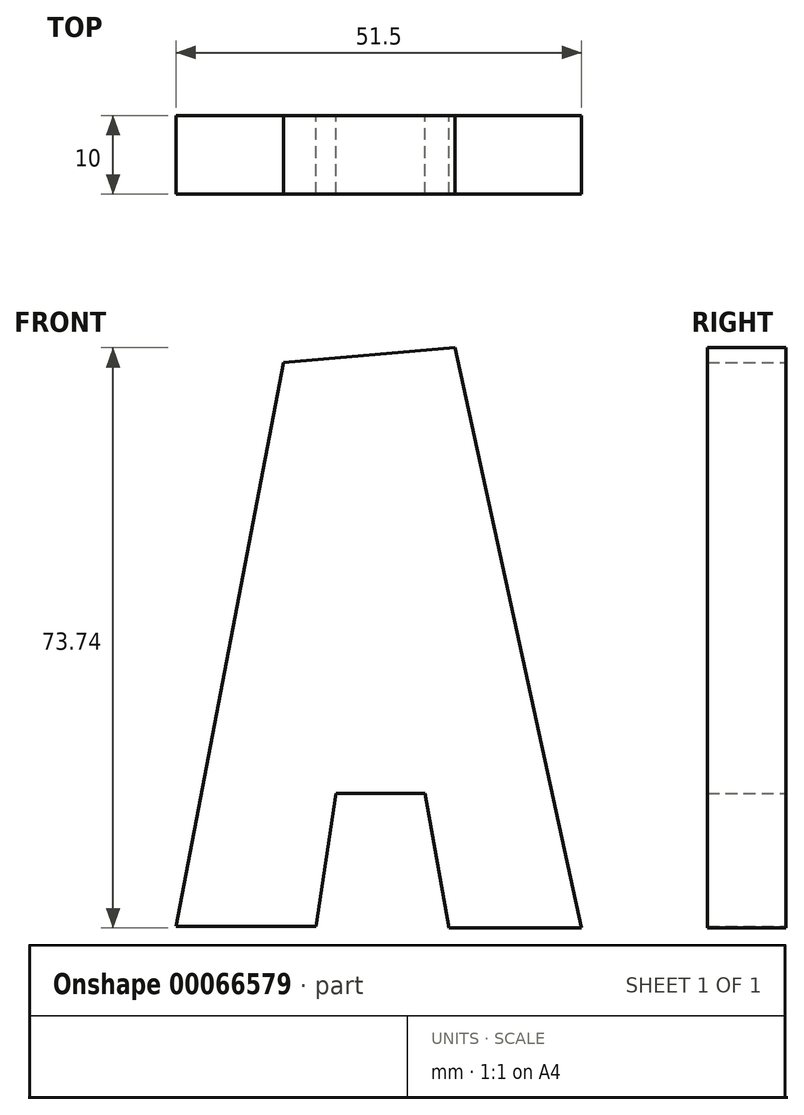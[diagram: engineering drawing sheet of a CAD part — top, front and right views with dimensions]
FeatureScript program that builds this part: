
annotation { "Feature Type Name" : "Feature", "Feature Type Description" : "" }
export const myFeature = defineFeature(function(context is Context, id is Id, definition is map)
    precondition{}
    {
        {
            var Q0;
            Q0=qCreatedBy(makeId("Front.planeOp"),FACE);
            var sketch = newSketch(context, id + "F0", { "sketchPlane" : qUnion([Q0])});
            skLineSegment(sketch, "E0", {"start": v(-11.08, 33.6) * mm, "end": v(-24.7, -37.98) * mm});
            skLineSegment(sketch, "E1", {"start": v(-24.7, -37.98) * mm, "end": v(-6.93, -37.98) * mm});
            skLineSegment(sketch, "E2", {"start": v(-6.93, -37.98) * mm, "end": v(-4.39, -21.13) * mm});
            skLineSegment(sketch, "E3", {"start": v(-4.39, -21.13) * mm, "end": v(6.93, -21.13) * mm});
            skLineSegment(sketch, "E4", {"start": v(6.93, -21.13) * mm, "end": v(9.93, -38.22) * mm});
            skLineSegment(sketch, "E5", {"start": v(9.93, -38.22) * mm, "end": v(26.79, -38.22) * mm});
            skLineSegment(sketch, "E6", {"start": v(26.79, -38.22) * mm, "end": v(10.74, 35.52) * mm});
            skLineSegment(sketch, "E7", {"start": v(-11.08, 33.6) * mm, "end": v(10.74, 35.52) * mm});
            skSolve(sketch);
        }
        {
            var Q0;
            Q0 = qSketchRegion(id + "F0", true);
            extrude(context, id + "F1", {"entities" : qUnion([Q0]), "depth" : 10 * mm});
        }
    });
